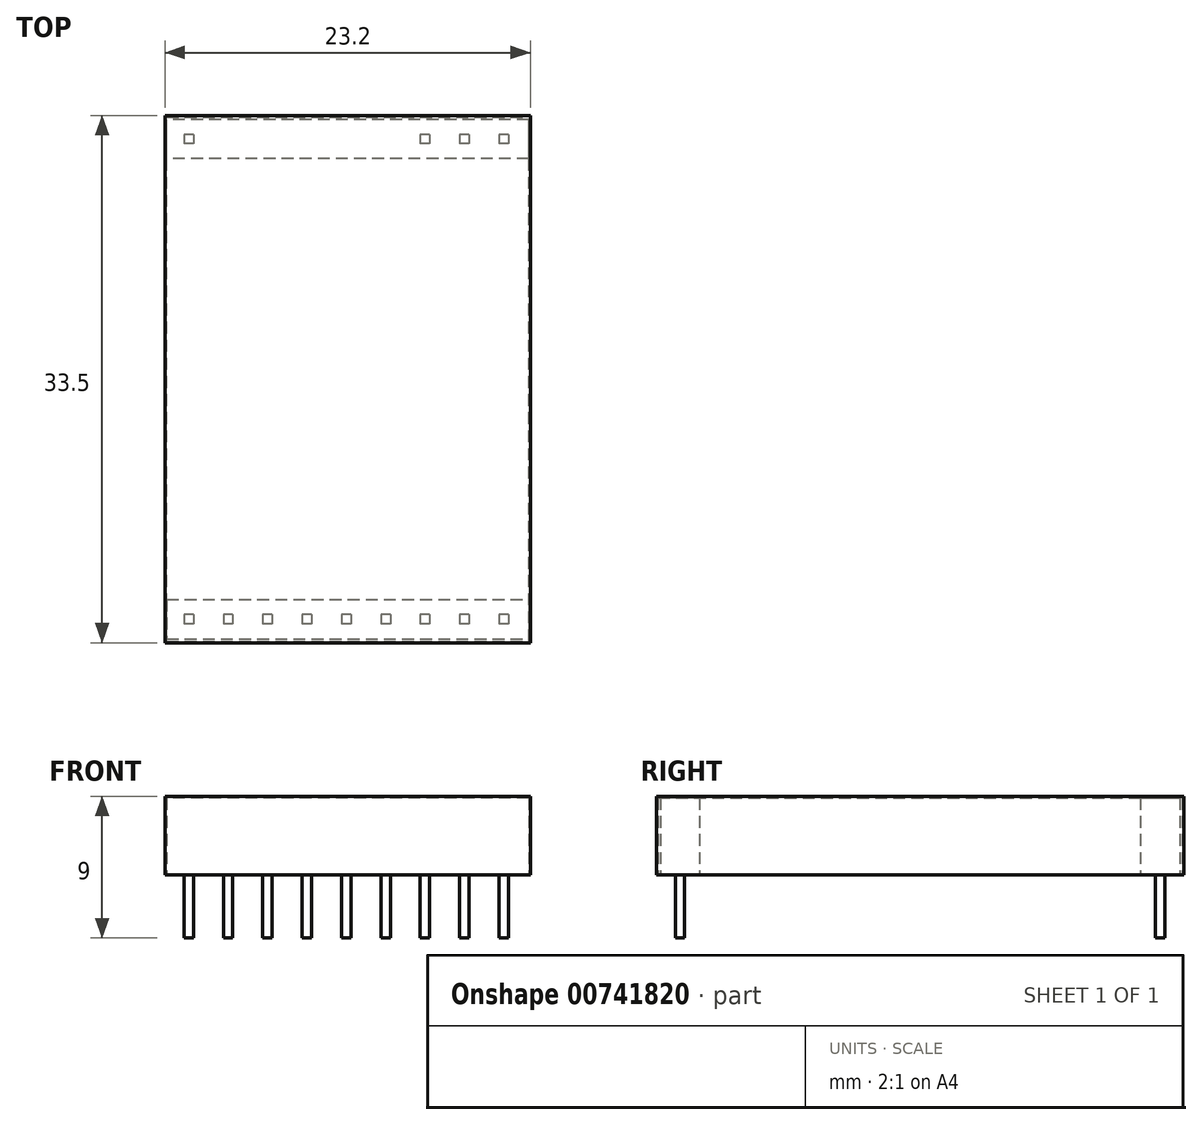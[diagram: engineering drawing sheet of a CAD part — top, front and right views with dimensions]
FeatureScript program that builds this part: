
annotation { "Feature Type Name" : "Feature", "Feature Type Description" : "" }
export const myFeature = defineFeature(function(context is Context, id is Id, definition is map)
    precondition{}
    {
        {
            var Q0;
            Q0=qCreatedBy(makeId("Top.planeOp"),FACE);
            var sketch = newSketch(context, id + "F0", { "sketchPlane" : qUnion([Q0])});
            skLineSegment(sketch, "E0.bottom", {"start": v(-12.32, -11.83) * mm, "end": v(10.88, -11.83) * mm});
            skLineSegment(sketch, "E0.top", {"start": v(-12.32, 21.67) * mm, "end": v(10.88, 21.67) * mm});
            skLineSegment(sketch, "E0.left", {"start": v(-12.32, -11.83) * mm, "end": v(-12.32, 21.67) * mm});
            skLineSegment(sketch, "E0.right", {"start": v(10.88, -11.83) * mm, "end": v(10.88, 21.67) * mm});
            skPoint(sketch, "E1.0", {"position": v(-10.82, 20.17) * mm});
            skPoint(sketch, "E2.0", {"position": v(-10.82, -10.33) * mm});
            skPoint(sketch, "E3.0", {"position": v(9.18, 20.17) * mm});
            skPoint(sketch, "E4.0", {"position": v(6.68, 20.17) * mm});
            skPoint(sketch, "E5.0", {"position": v(4.18, 20.17) * mm});
            skPoint(sketch, "E6.0", {"position": v(9.18, -10.33) * mm});
            skPoint(sketch, "E7.0", {"position": v(6.68, -10.33) * mm});
            skPoint(sketch, "E8.0", {"position": v(4.18, -10.33) * mm});
            skPoint(sketch, "E9.0", {"position": v(1.68, -10.33) * mm});
            skPoint(sketch, "E10.0", {"position": v(-0.82, -10.33) * mm});
            skPoint(sketch, "E11.0", {"position": v(-3.32, -10.33) * mm});
            skPoint(sketch, "E12.0", {"position": v(-5.82, -10.33) * mm});
            skPoint(sketch, "E13.0", {"position": v(-8.32, -10.33) * mm});
            skLineSegment(sketch, "E14.bottom", {"start": v(10.78, 18.92) * mm, "end": v(-12.22, 18.92) * mm});
            skLineSegment(sketch, "E14.top", {"start": v(10.78, 21.42) * mm, "end": v(-12.22, 21.42) * mm});
            skLineSegment(sketch, "E14.left", {"start": v(10.78, 18.92) * mm, "end": v(10.78, 21.42) * mm});
            skLineSegment(sketch, "E14.right", {"start": v(-12.22, 18.92) * mm, "end": v(-12.22, 21.42) * mm});
            skLineSegment(sketch, "E15.bottom", {"start": v(-12.22, -9.08) * mm, "end": v(10.78, -9.08) * mm});
            skLineSegment(sketch, "E15.top", {"start": v(-12.22, -11.58) * mm, "end": v(10.78, -11.58) * mm});
            skLineSegment(sketch, "E15.left", {"start": v(-12.22, -9.08) * mm, "end": v(-12.22, -11.58) * mm});
            skLineSegment(sketch, "E15.right", {"start": v(10.78, -9.08) * mm, "end": v(10.78, -11.58) * mm});
            skLineSegment(sketch, "E16", {"start": v(-10.82, -10.33) * mm, "end": v(9.18, -10.33) * mm, "construction": true});
            skLineSegment(sketch, "E17", {"start": v(-0.72, -11.83) * mm, "end": v(-0.72, 21.67) * mm, "construction": true});
            skLineSegment(sketch, "E18", {"start": v(-10.82, 20.17) * mm, "end": v(9.18, 20.17) * mm, "construction": true});
            skLineSegment(sketch, "E19.bottom", {"start": v(9.48, -10.03) * mm, "end": v(8.88, -10.03) * mm});
            skLineSegment(sketch, "E19.top", {"start": v(9.48, -10.63) * mm, "end": v(8.88, -10.63) * mm});
            skLineSegment(sketch, "E19.left", {"start": v(9.48, -10.03) * mm, "end": v(9.48, -10.63) * mm});
            skLineSegment(sketch, "E19.right", {"start": v(8.88, -10.03) * mm, "end": v(8.88, -10.63) * mm});
            skLineSegment(sketch, "E20.bottom", {"start": v(6.98, -10.03) * mm, "end": v(6.38, -10.03) * mm});
            skLineSegment(sketch, "E20.top", {"start": v(6.98, -10.63) * mm, "end": v(6.38, -10.63) * mm});
            skLineSegment(sketch, "E20.left", {"start": v(6.98, -10.03) * mm, "end": v(6.98, -10.63) * mm});
            skLineSegment(sketch, "E20.right", {"start": v(6.38, -10.03) * mm, "end": v(6.38, -10.63) * mm});
            skLineSegment(sketch, "E21.bottom", {"start": v(4.48, -10.03) * mm, "end": v(3.88, -10.03) * mm});
            skLineSegment(sketch, "E21.top", {"start": v(4.48, -10.63) * mm, "end": v(3.88, -10.63) * mm});
            skLineSegment(sketch, "E21.left", {"start": v(4.48, -10.03) * mm, "end": v(4.48, -10.63) * mm});
            skLineSegment(sketch, "E21.right", {"start": v(3.88, -10.03) * mm, "end": v(3.88, -10.63) * mm});
            skLineSegment(sketch, "E22.bottom", {"start": v(1.98, -10.03) * mm, "end": v(1.38, -10.03) * mm});
            skLineSegment(sketch, "E22.top", {"start": v(1.98, -10.63) * mm, "end": v(1.38, -10.63) * mm});
            skLineSegment(sketch, "E22.left", {"start": v(1.98, -10.03) * mm, "end": v(1.98, -10.63) * mm});
            skLineSegment(sketch, "E22.right", {"start": v(1.38, -10.03) * mm, "end": v(1.38, -10.63) * mm});
            skLineSegment(sketch, "E23.bottom", {"start": v(-0.52, -10.03) * mm, "end": v(-1.12, -10.03) * mm});
            skLineSegment(sketch, "E23.top", {"start": v(-0.52, -10.63) * mm, "end": v(-1.12, -10.63) * mm});
            skLineSegment(sketch, "E23.left", {"start": v(-0.52, -10.03) * mm, "end": v(-0.52, -10.63) * mm});
            skLineSegment(sketch, "E23.right", {"start": v(-1.12, -10.03) * mm, "end": v(-1.12, -10.63) * mm});
            skLineSegment(sketch, "E24.bottom", {"start": v(-3.02, -10.03) * mm, "end": v(-3.62, -10.03) * mm});
            skLineSegment(sketch, "E24.top", {"start": v(-3.02, -10.63) * mm, "end": v(-3.62, -10.63) * mm});
            skLineSegment(sketch, "E24.left", {"start": v(-3.02, -10.03) * mm, "end": v(-3.02, -10.63) * mm});
            skLineSegment(sketch, "E24.right", {"start": v(-3.62, -10.03) * mm, "end": v(-3.62, -10.63) * mm});
            skLineSegment(sketch, "E25.bottom", {"start": v(-5.52, -10.03) * mm, "end": v(-6.12, -10.03) * mm});
            skLineSegment(sketch, "E25.top", {"start": v(-5.52, -10.63) * mm, "end": v(-6.12, -10.63) * mm});
            skLineSegment(sketch, "E25.left", {"start": v(-5.52, -10.03) * mm, "end": v(-5.52, -10.63) * mm});
            skLineSegment(sketch, "E25.right", {"start": v(-6.12, -10.03) * mm, "end": v(-6.12, -10.63) * mm});
            skLineSegment(sketch, "E26.bottom", {"start": v(-8.02, -10.03) * mm, "end": v(-8.62, -10.03) * mm});
            skLineSegment(sketch, "E26.top", {"start": v(-8.02, -10.63) * mm, "end": v(-8.62, -10.63) * mm});
            skLineSegment(sketch, "E26.left", {"start": v(-8.02, -10.03) * mm, "end": v(-8.02, -10.63) * mm});
            skLineSegment(sketch, "E26.right", {"start": v(-8.62, -10.03) * mm, "end": v(-8.62, -10.63) * mm});
            skLineSegment(sketch, "E27.bottom", {"start": v(-10.52, -10.03) * mm, "end": v(-11.12, -10.03) * mm});
            skLineSegment(sketch, "E27.top", {"start": v(-10.52, -10.63) * mm, "end": v(-11.12, -10.63) * mm});
            skLineSegment(sketch, "E27.left", {"start": v(-10.52, -10.03) * mm, "end": v(-10.52, -10.63) * mm});
            skLineSegment(sketch, "E27.right", {"start": v(-11.12, -10.03) * mm, "end": v(-11.12, -10.63) * mm});
            skLineSegment(sketch, "E28.bottom", {"start": v(9.48, 20.47) * mm, "end": v(8.88, 20.47) * mm});
            skLineSegment(sketch, "E28.top", {"start": v(9.48, 19.87) * mm, "end": v(8.88, 19.87) * mm});
            skLineSegment(sketch, "E28.left", {"start": v(9.48, 20.47) * mm, "end": v(9.48, 19.87) * mm});
            skLineSegment(sketch, "E28.right", {"start": v(8.88, 20.47) * mm, "end": v(8.88, 19.87) * mm});
            skLineSegment(sketch, "E29.bottom", {"start": v(6.98, 20.47) * mm, "end": v(6.38, 20.47) * mm});
            skLineSegment(sketch, "E29.top", {"start": v(6.98, 19.87) * mm, "end": v(6.38, 19.87) * mm});
            skLineSegment(sketch, "E29.left", {"start": v(6.98, 20.47) * mm, "end": v(6.98, 19.87) * mm});
            skLineSegment(sketch, "E29.right", {"start": v(6.38, 20.47) * mm, "end": v(6.38, 19.87) * mm});
            skLineSegment(sketch, "E30.bottom", {"start": v(4.48, 20.47) * mm, "end": v(3.88, 20.47) * mm});
            skLineSegment(sketch, "E30.top", {"start": v(4.48, 19.87) * mm, "end": v(3.88, 19.87) * mm});
            skLineSegment(sketch, "E30.left", {"start": v(4.48, 20.47) * mm, "end": v(4.48, 19.87) * mm});
            skLineSegment(sketch, "E30.right", {"start": v(3.88, 20.47) * mm, "end": v(3.88, 19.87) * mm});
            skLineSegment(sketch, "E31.bottom", {"start": v(-10.52, 20.47) * mm, "end": v(-11.12, 20.47) * mm});
            skLineSegment(sketch, "E31.top", {"start": v(-10.52, 19.87) * mm, "end": v(-11.12, 19.87) * mm});
            skLineSegment(sketch, "E31.left", {"start": v(-10.52, 20.47) * mm, "end": v(-10.52, 19.87) * mm});
            skLineSegment(sketch, "E31.right", {"start": v(-11.12, 20.47) * mm, "end": v(-11.12, 19.87) * mm});
            skSolve(sketch);
        }
        {
            var Q0;
            Q0=makeQuery(id+"F0.imprint","IMPRINT",FACE,{"disambiguationData":[TD([[makeQuery(id+"F0.imprint","IMPRINT",EDGE,{"derivedFrom":sQuery(id+"F0.wireOp",EDGE,"E0.bottom")}),1.0]])]});
            var Q1;
            Q1=makeQuery(id+"F0.imprint","IMPRINT",FACE,{"disambiguationData":[TD([[makeQuery(id+"F0.imprint","IMPRINT",EDGE,{"derivedFrom":sQuery(id+"F0.wireOp",EDGE,"E14.bottom")}),-1.0]])]});
            var Q2;
            Q2=makeQuery(id+"F0.imprint","IMPRINT",FACE,{"disambiguationData":[TD([[makeQuery(id+"F0.imprint","IMPRINT",EDGE,{"derivedFrom":sQuery(id+"F0.wireOp",EDGE,"E15.bottom")}),-1.0]])]});
            var Q3;
            Q3=makeQuery(id+"F0.imprint","IMPRINT",FACE,{"disambiguationData":[TD([[makeQuery(id+"F0.imprint","IMPRINT",EDGE,{"derivedFrom":sQuery(id+"F0.wireOp",EDGE,"E21.bottom")}),1.0]])]});
            var Q4;
            Q4=makeQuery(id+"F0.imprint","IMPRINT",FACE,{"disambiguationData":[TD([[makeQuery(id+"F0.imprint","IMPRINT",EDGE,{"derivedFrom":sQuery(id+"F0.wireOp",EDGE,"E22.bottom")}),1.0]])]});
            var Q5;
            Q5=makeQuery(id+"F0.imprint","IMPRINT",FACE,{"disambiguationData":[TD([[makeQuery(id+"F0.imprint","IMPRINT",EDGE,{"derivedFrom":sQuery(id+"F0.wireOp",EDGE,"E25.bottom")}),1.0]])]});
            var Q6;
            Q6=makeQuery(id+"F0.imprint","IMPRINT",FACE,{"disambiguationData":[TD([[makeQuery(id+"F0.imprint","IMPRINT",EDGE,{"derivedFrom":sQuery(id+"F0.wireOp",EDGE,"E26.bottom")}),1.0]])]});
            var Q7;
            Q7=makeQuery(id+"F0.imprint","IMPRINT",FACE,{"disambiguationData":[TD([[makeQuery(id+"F0.imprint","IMPRINT",EDGE,{"derivedFrom":sQuery(id+"F0.wireOp",EDGE,"E29.bottom")}),1.0]])]});
            var Q8;
            Q8=makeQuery(id+"F0.imprint","IMPRINT",FACE,{"disambiguationData":[TD([[makeQuery(id+"F0.imprint","IMPRINT",EDGE,{"derivedFrom":sQuery(id+"F0.wireOp",EDGE,"E30.bottom")}),1.0]])]});
            var Q9;
            Q9=makeQuery(id+"F0.imprint","IMPRINT",FACE,{"disambiguationData":[TD([[makeQuery(id+"F0.imprint","IMPRINT",EDGE,{"derivedFrom":sQuery(id+"F0.wireOp",EDGE,"E19.bottom")}),1.0]])]});
            var Q10;
            Q10=makeQuery(id+"F0.imprint","IMPRINT",FACE,{"disambiguationData":[TD([[makeQuery(id+"F0.imprint","IMPRINT",EDGE,{"derivedFrom":sQuery(id+"F0.wireOp",EDGE,"E20.bottom")}),1.0]])]});
            var Q11;
            Q11=makeQuery(id+"F0.imprint","IMPRINT",FACE,{"disambiguationData":[TD([[makeQuery(id+"F0.imprint","IMPRINT",EDGE,{"derivedFrom":sQuery(id+"F0.wireOp",EDGE,"E23.bottom")}),1.0]])]});
            var Q12;
            Q12=makeQuery(id+"F0.imprint","IMPRINT",FACE,{"disambiguationData":[TD([[makeQuery(id+"F0.imprint","IMPRINT",EDGE,{"derivedFrom":sQuery(id+"F0.wireOp",EDGE,"E24.bottom")}),1.0]])]});
            var Q13;
            Q13=makeQuery(id+"F0.imprint","IMPRINT",FACE,{"disambiguationData":[TD([[makeQuery(id+"F0.imprint","IMPRINT",EDGE,{"derivedFrom":sQuery(id+"F0.wireOp",EDGE,"E27.bottom")}),1.0]])]});
            var Q14;
            Q14=makeQuery(id+"F0.imprint","IMPRINT",FACE,{"disambiguationData":[TD([[makeQuery(id+"F0.imprint","IMPRINT",EDGE,{"derivedFrom":sQuery(id+"F0.wireOp",EDGE,"E28.bottom")}),1.0]])]});
            var Q15;
            Q15=makeQuery(id+"F0.imprint","IMPRINT",FACE,{"disambiguationData":[TD([[makeQuery(id+"F0.imprint","IMPRINT",EDGE,{"derivedFrom":sQuery(id+"F0.wireOp",EDGE,"E31.bottom")}),1.0]])]});
            extrude(context, id + "F1", {"entities" : qUnion([Q0, Q1, Q2, Q3, Q4, Q5, Q6, Q7, Q8, Q9, Q10, Q11, Q12, Q13, Q14, Q15]), "depth" : 5 * mm, "offsetDistance" : 25 * mm});
        }
        {
            var Q0;
            Q0=makeQuery(id+"F1.opExtrude","CAP_FACE",FACE,{"disambiguationData":[OSD([sQuery(id+"F0.wireOp",EDGE,"E0.bottom"),sQuery(id+"F0.wireOp",EDGE,"E0.top"),sQuery(id+"F0.wireOp",EDGE,"E0.left"),sQuery(id+"F0.wireOp",EDGE,"E0.right")])],"isStart":true});
            shell(context, id + "F2", {"entities" : qUnion([Q0]), "thickness" : .1 * mm});
        }
        {
            var Q0;
            Q0=makeQuery(id+"F0.imprint","IMPRINT",FACE,{"disambiguationData":[TD([[makeQuery(id+"F0.imprint","IMPRINT",EDGE,{"derivedFrom":sQuery(id+"F0.wireOp",EDGE,"E31.bottom")}),1.0]])]});
            var Q1;
            Q1=makeQuery(id+"F0.imprint","IMPRINT",FACE,{"disambiguationData":[TD([[makeQuery(id+"F0.imprint","IMPRINT",EDGE,{"derivedFrom":sQuery(id+"F0.wireOp",EDGE,"E30.bottom")}),1.0]])]});
            var Q2;
            Q2=makeQuery(id+"F0.imprint","IMPRINT",FACE,{"disambiguationData":[TD([[makeQuery(id+"F0.imprint","IMPRINT",EDGE,{"derivedFrom":sQuery(id+"F0.wireOp",EDGE,"E29.bottom")}),1.0]])]});
            var Q3;
            Q3=makeQuery(id+"F0.imprint","IMPRINT",FACE,{"disambiguationData":[TD([[makeQuery(id+"F0.imprint","IMPRINT",EDGE,{"derivedFrom":sQuery(id+"F0.wireOp",EDGE,"E28.bottom")}),1.0]])]});
            var Q4;
            Q4=makeQuery(id+"F0.imprint","IMPRINT",FACE,{"disambiguationData":[TD([[makeQuery(id+"F0.imprint","IMPRINT",EDGE,{"derivedFrom":sQuery(id+"F0.wireOp",EDGE,"E14.bottom")}),-1.0]])]});
            var Q5;
            Q5=makeQuery(id+"F0.imprint","IMPRINT",FACE,{"disambiguationData":[TD([[makeQuery(id+"F0.imprint","IMPRINT",EDGE,{"derivedFrom":sQuery(id+"F0.wireOp",EDGE,"E19.bottom")}),1.0]])]});
            var Q6;
            Q6=makeQuery(id+"F0.imprint","IMPRINT",FACE,{"disambiguationData":[TD([[makeQuery(id+"F0.imprint","IMPRINT",EDGE,{"derivedFrom":sQuery(id+"F0.wireOp",EDGE,"E20.bottom")}),1.0]])]});
            var Q7;
            Q7=makeQuery(id+"F0.imprint","IMPRINT",FACE,{"disambiguationData":[TD([[makeQuery(id+"F0.imprint","IMPRINT",EDGE,{"derivedFrom":sQuery(id+"F0.wireOp",EDGE,"E21.bottom")}),1.0]])]});
            var Q8;
            Q8=makeQuery(id+"F0.imprint","IMPRINT",FACE,{"disambiguationData":[TD([[makeQuery(id+"F0.imprint","IMPRINT",EDGE,{"derivedFrom":sQuery(id+"F0.wireOp",EDGE,"E22.bottom")}),1.0]])]});
            var Q9;
            Q9=makeQuery(id+"F0.imprint","IMPRINT",FACE,{"disambiguationData":[TD([[makeQuery(id+"F0.imprint","IMPRINT",EDGE,{"derivedFrom":sQuery(id+"F0.wireOp",EDGE,"E23.bottom")}),1.0]])]});
            var Q10;
            Q10=makeQuery(id+"F0.imprint","IMPRINT",FACE,{"disambiguationData":[TD([[makeQuery(id+"F0.imprint","IMPRINT",EDGE,{"derivedFrom":sQuery(id+"F0.wireOp",EDGE,"E24.bottom")}),1.0]])]});
            var Q11;
            Q11=makeQuery(id+"F0.imprint","IMPRINT",FACE,{"disambiguationData":[TD([[makeQuery(id+"F0.imprint","IMPRINT",EDGE,{"derivedFrom":sQuery(id+"F0.wireOp",EDGE,"E25.bottom")}),1.0]])]});
            var Q12;
            Q12=makeQuery(id+"F0.imprint","IMPRINT",FACE,{"disambiguationData":[TD([[makeQuery(id+"F0.imprint","IMPRINT",EDGE,{"derivedFrom":sQuery(id+"F0.wireOp",EDGE,"E26.bottom")}),1.0]])]});
            var Q13;
            Q13=makeQuery(id+"F0.imprint","IMPRINT",FACE,{"disambiguationData":[TD([[makeQuery(id+"F0.imprint","IMPRINT",EDGE,{"derivedFrom":sQuery(id+"F0.wireOp",EDGE,"E27.bottom")}),1.0]])]});
            var Q14;
            Q14=makeQuery(id+"F0.imprint","IMPRINT",FACE,{"disambiguationData":[TD([[makeQuery(id+"F0.imprint","IMPRINT",EDGE,{"derivedFrom":sQuery(id+"F0.wireOp",EDGE,"E15.bottom")}),-1.0]])]});
            var Q15;
            Q15=makeQuery(id+"F2.opShell","OFFSET_FACE",FACE,{"disambiguationData":[OSD([sQuery(id+"F0.wireOp",EDGE,"E0.bottom"),sQuery(id+"F0.wireOp",EDGE,"E0.top"),sQuery(id+"F0.wireOp",EDGE,"E0.left"),sQuery(id+"F0.wireOp",EDGE,"E0.right")])]});
            extrude(context, id + "F3", {"entities" : qUnion([Q0, Q1, Q2, Q3, Q4, Q5, Q6, Q7, Q8, Q9, Q10, Q11, Q12, Q13, Q14]), "endBound" : BoundingType.UP_TO_SURFACE, "depth" : 4 * mm, "endBoundEntityFace" : qUnion([Q15]), "offsetDistance" : 25 * mm});
        }
        {
            var Q0;
            Q0=makeQuery(id+"F0.imprint","IMPRINT",FACE,{"disambiguationData":[TD([[makeQuery(id+"F0.imprint","IMPRINT",EDGE,{"derivedFrom":sQuery(id+"F0.wireOp",EDGE,"E20.bottom")}),1.0]])]});
            var Q1;
            Q1=makeQuery(id+"F0.imprint","IMPRINT",FACE,{"disambiguationData":[TD([[makeQuery(id+"F0.imprint","IMPRINT",EDGE,{"derivedFrom":sQuery(id+"F0.wireOp",EDGE,"E21.bottom")}),1.0]])]});
            var Q2;
            Q2=makeQuery(id+"F0.imprint","IMPRINT",FACE,{"disambiguationData":[TD([[makeQuery(id+"F0.imprint","IMPRINT",EDGE,{"derivedFrom":sQuery(id+"F0.wireOp",EDGE,"E22.bottom")}),1.0]])]});
            var Q3;
            Q3=makeQuery(id+"F0.imprint","IMPRINT",FACE,{"disambiguationData":[TD([[makeQuery(id+"F0.imprint","IMPRINT",EDGE,{"derivedFrom":sQuery(id+"F0.wireOp",EDGE,"E23.bottom")}),1.0]])]});
            var Q4;
            Q4=makeQuery(id+"F0.imprint","IMPRINT",FACE,{"disambiguationData":[TD([[makeQuery(id+"F0.imprint","IMPRINT",EDGE,{"derivedFrom":sQuery(id+"F0.wireOp",EDGE,"E24.bottom")}),1.0]])]});
            var Q5;
            Q5=makeQuery(id+"F0.imprint","IMPRINT",FACE,{"disambiguationData":[TD([[makeQuery(id+"F0.imprint","IMPRINT",EDGE,{"derivedFrom":sQuery(id+"F0.wireOp",EDGE,"E25.bottom")}),1.0]])]});
            var Q6;
            Q6=makeQuery(id+"F0.imprint","IMPRINT",FACE,{"disambiguationData":[TD([[makeQuery(id+"F0.imprint","IMPRINT",EDGE,{"derivedFrom":sQuery(id+"F0.wireOp",EDGE,"E26.bottom")}),1.0]])]});
            var Q7;
            Q7=makeQuery(id+"F0.imprint","IMPRINT",FACE,{"disambiguationData":[TD([[makeQuery(id+"F0.imprint","IMPRINT",EDGE,{"derivedFrom":sQuery(id+"F0.wireOp",EDGE,"E19.bottom")}),1.0]])]});
            var Q8;
            Q8=makeQuery(id+"F0.imprint","IMPRINT",FACE,{"disambiguationData":[TD([[makeQuery(id+"F0.imprint","IMPRINT",EDGE,{"derivedFrom":sQuery(id+"F0.wireOp",EDGE,"E27.bottom")}),1.0]])]});
            var Q9;
            Q9=makeQuery(id+"F0.imprint","IMPRINT",FACE,{"disambiguationData":[TD([[makeQuery(id+"F0.imprint","IMPRINT",EDGE,{"derivedFrom":sQuery(id+"F0.wireOp",EDGE,"E31.bottom")}),1.0]])]});
            var Q10;
            Q10=makeQuery(id+"F0.imprint","IMPRINT",FACE,{"disambiguationData":[TD([[makeQuery(id+"F0.imprint","IMPRINT",EDGE,{"derivedFrom":sQuery(id+"F0.wireOp",EDGE,"E28.bottom")}),1.0]])]});
            var Q11;
            Q11=makeQuery(id+"F0.imprint","IMPRINT",FACE,{"disambiguationData":[TD([[makeQuery(id+"F0.imprint","IMPRINT",EDGE,{"derivedFrom":sQuery(id+"F0.wireOp",EDGE,"E29.bottom")}),1.0]])]});
            var Q12;
            Q12=makeQuery(id+"F0.imprint","IMPRINT",FACE,{"disambiguationData":[TD([[makeQuery(id+"F0.imprint","IMPRINT",EDGE,{"derivedFrom":sQuery(id+"F0.wireOp",EDGE,"E30.bottom")}),1.0]])]});
            extrude(context, id + "F4", {"entities" : qUnion([Q0, Q1, Q2, Q3, Q4, Q5, Q6, Q7, Q8, Q9, Q10, Q11, Q12]), "oppositeDirection" : true, "depth" : 4 * mm, "offsetDistance" : 25 * mm});
        }
    });
